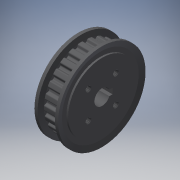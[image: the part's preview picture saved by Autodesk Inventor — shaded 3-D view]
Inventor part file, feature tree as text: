
AUTODESK INVENTOR PART (.ipt)
format: ipt  version: 2017 (Build 210142000, 142)  size: 589,824 bytes
history: native  units: mm
features: other x14, revolve x4, hole x2, extrude x2, thread x2, sketch x2, pattern_linear x1
ambient origin geometry x8: Origin, YZ Plane, XZ Plane, XY Plane, X Axis, Y Axis, Z Axis, Center Point
bodies: Solid1 (feature_tree)
feature tree (27):
  revolve  "Revolution1"  [1 undecoded]
  hole  "Hole1"  [1 undecoded]
  extrude  "Extrusion1"  TaperAngle=360.0deg  [1 undecoded]
  extrude  "Extrusion2"  TaperAngle=360.0deg  [1 undecoded]
  revolve  "Revolution2"  [1 undecoded]
  revolve  "Revolution3"  Angle=360.0deg
  thread  "Thread1"  [1 undecoded]
  revolve  "Revolution4"  [1 undecoded]
  thread  "Thread2"  [1 undecoded]
  hole  "Hole2"  [1 undecoded]
  pattern_linear  "Rectangular Pattern1"  [2 undecoded]
  other  "to_screw1_XY"
  other  "to_screw1_YZ"
  other  "to_screw1_ZX"
  other  "to_screw1_X"
  other  "to_screw1_Y"
  other  "to_screw1_Z"
  other  "to_screw1_Center"
  other  "to_screw2_XY"
  other  "to_screw2_YZ"
  other  "to_screw2_ZX"
  other  "to_screw2_X"
  other  "to_screw2_Y"
  other  "to_screw2_Z"
  other  "to_screw2_Center"
  sketch  "Sketch2"  dims[d0=360.0deg]
  sketch  "Sketch8"  dims[d1=8.0mm d2=6.0mm d3=4.0mm d4=2.0mm d5=90.0deg d6=12.5mm d7=0.0mm d8=7.5mm d9=0.0mm d10=12.5mm d11=0.0mm d12=360.0deg d13=360.0deg d14=14.56mm d15=0.0mm d16=360.0deg d17=15.96mm d18=0.0mm d19=2.459mm d20=6.2705mm d21=3.0mm d22=2.0mm d23=90.0deg d24=8.790148mm d25=120.0deg d26=20.0mm d28=14.142136mm d29=20.0mm d31=14.142136mm d32=0.0mm]
note: 11 required parameter values undecoded (feature->parameter linkage not recoverable at this tier; creation-order binding heuristic only, values carry confidence <= 0.55)